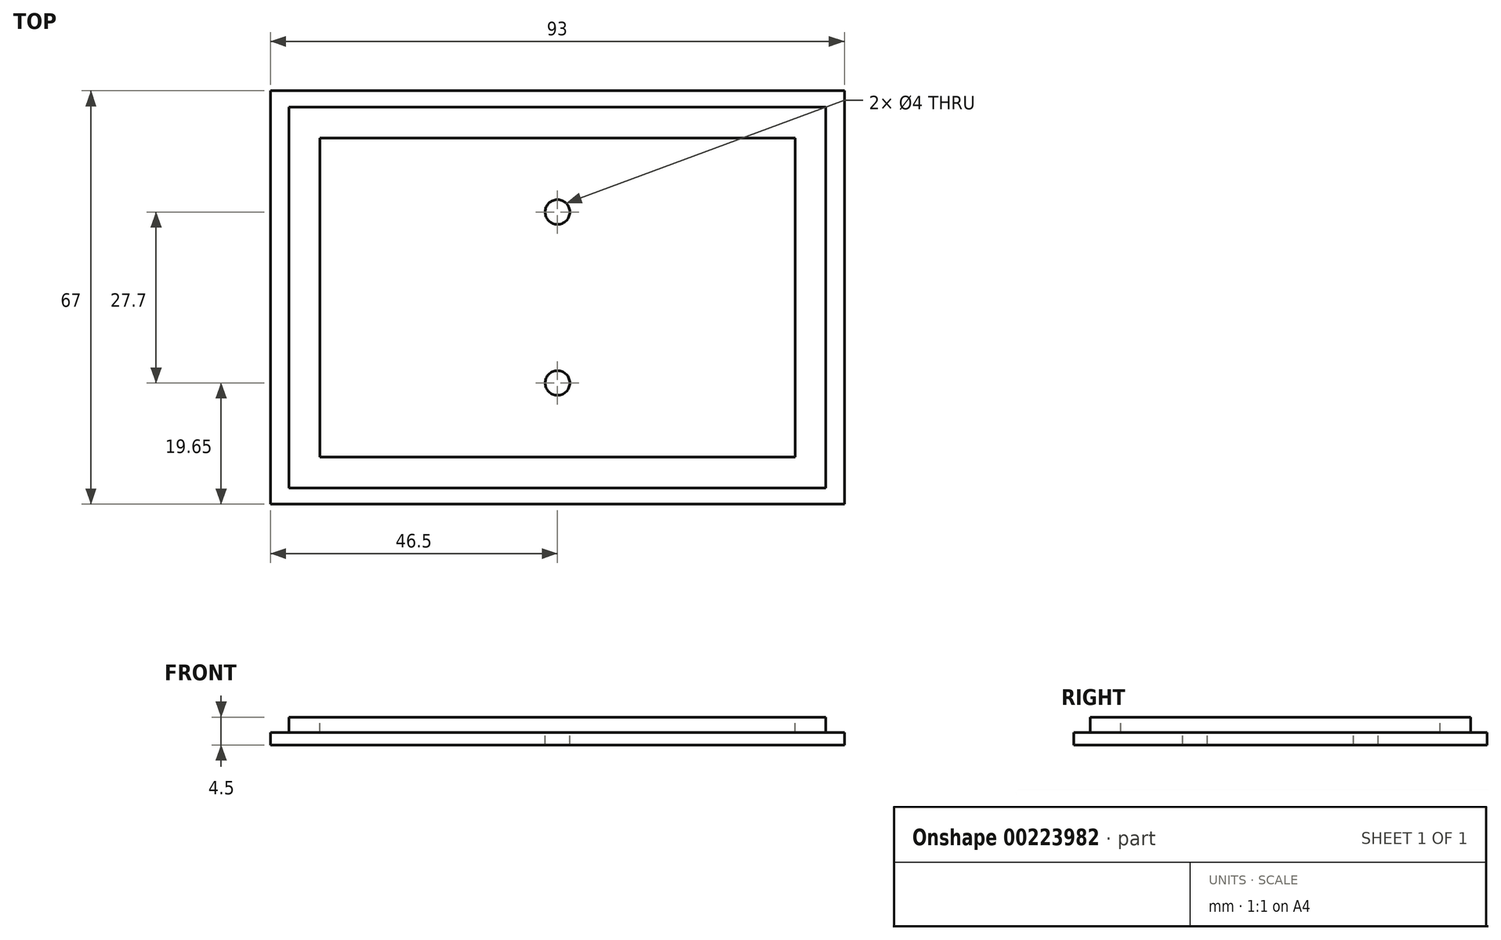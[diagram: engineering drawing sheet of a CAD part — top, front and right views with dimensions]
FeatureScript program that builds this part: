
annotation { "Feature Type Name" : "Feature", "Feature Type Description" : "" }
export const myFeature = defineFeature(function(context is Context, id is Id, definition is map)
    precondition{}
    {
        {
            var Q0;
            Q0=qCreatedBy(makeId("Top.planeOp"),FACE);
            var sketch = newSketch(context, id + "F0", { "sketchPlane" : qUnion([Q0])});
            skLineSegment(sketch, "E0.bottom", {"start": v(46.5, -33.5) * mm, "end": v(-46.5, -33.5) * mm});
            skLineSegment(sketch, "E0.top", {"start": v(46.5, 33.5) * mm, "end": v(-46.5, 33.5) * mm});
            skLineSegment(sketch, "E0.left", {"start": v(46.5, -33.5) * mm, "end": v(46.5, 33.5) * mm});
            skLineSegment(sketch, "E0.right", {"start": v(-46.5, -33.5) * mm, "end": v(-46.5, 33.5) * mm});
            skPoint(sketch, "E0.middle", {"position": v(0, 0) * mm});
            skSolve(sketch);
        }
        {
            var Q0;
            Q0 = qSketchRegion(id + "F0", true);
            extrude(context, id + "F1", {"entities" : qUnion([Q0]), "depth" : 2 * mm});
        }
        {
            var Q0;
            Q0=makeQuery(id+"F1.opExtrude","CAP_FACE",FACE,{"disambiguationData":[OSD([sQuery(id+"F0.wireOp",EDGE,"E0.bottom"),sQuery(id+"F0.wireOp",EDGE,"E0.top"),sQuery(id+"F0.wireOp",EDGE,"E0.left"),sQuery(id+"F0.wireOp",EDGE,"E0.right")])],"isStart":false});
            var sketch = newSketch(context, id + "F2", { "sketchPlane" : qUnion([Q0])});
            skLineSegment(sketch, "E1.bottom", {"start": v(43.5, -30.85) * mm, "end": v(-43.5, -30.85) * mm});
            skLineSegment(sketch, "E1.top", {"start": v(43.5, 30.85) * mm, "end": v(-43.5, 30.85) * mm});
            skLineSegment(sketch, "E1.left", {"start": v(43.5, -30.85) * mm, "end": v(43.5, 30.85) * mm});
            skLineSegment(sketch, "E1.right", {"start": v(-43.5, -30.85) * mm, "end": v(-43.5, 30.85) * mm});
            skPoint(sketch, "E1.middle", {"position": v(0, 0) * mm});
            skSolve(sketch);
        }
        {
            var Q0;
            Q0 = qSketchRegion(id + "F2", true);
            extrude(context, id + "F3", {"entities" : qUnion([Q0]), "operationType" : NewBodyOperationType.ADD, "depth" : 2.5 * mm});
        }
        {
            var Q0;
            Q0=makeQuery(id+"F3.opExtrude","CAP_FACE",FACE,{"disambiguationData":[OSD([sQuery(id+"F2.wireOp",EDGE,"E1.bottom"),sQuery(id+"F2.wireOp",EDGE,"E1.top"),sQuery(id+"F2.wireOp",EDGE,"E1.left"),sQuery(id+"F2.wireOp",EDGE,"E1.right")])],"isStart":false});
            var sketch = newSketch(context, id + "F4", { "sketchPlane" : qUnion([Q0])});
            skCircle(sketch, "E2", {"center": v(0, 13.85) * mm, "radius": 2 * mm});
            skCircle(sketch, "E3", {"center": v(0, -13.85) * mm, "radius": 2 * mm});
            skLineSegment(sketch, "E4", {"start": v(0, 30.85) * mm, "end": v(0, 15.85) * mm, "construction": true});
            skLineSegment(sketch, "E5", {"start": v(0, -30.85) * mm, "end": v(0, -15.85) * mm, "construction": true});
            skSolve(sketch);
        }
        {
            var Q0;
            Q0 = qSketchRegion(id + "F4", true);
            extrude(context, id + "F5", {"entities" : qUnion([Q0]), "operationType" : NewBodyOperationType.REMOVE, "endBound" : BoundingType.THROUGH_ALL, "oppositeDirection" : true, "depth" : 25 * mm});
        }
        {
            var Q0;
            Q0=makeQuery(id+"F3.opExtrude","CAP_FACE",FACE,{"disambiguationData":[OSD([sQuery(id+"F2.wireOp",EDGE,"E1.bottom"),sQuery(id+"F2.wireOp",EDGE,"E1.top"),sQuery(id+"F2.wireOp",EDGE,"E1.left"),sQuery(id+"F2.wireOp",EDGE,"E1.right")])],"isStart":false});
            var sketch = newSketch(context, id + "F6", { "sketchPlane" : qUnion([Q0])});
            skLineSegment(sketch, "E6.0", {"start": v(38.5, -25.85) * mm, "end": v(38.5, 25.85) * mm});
            skLineSegment(sketch, "E6.1", {"start": v(-38.5, -25.85) * mm, "end": v(38.5, -25.85) * mm});
            skLineSegment(sketch, "E6.2", {"start": v(-38.5, 25.85) * mm, "end": v(-38.5, -25.85) * mm});
            skLineSegment(sketch, "E6.3", {"start": v(38.5, 25.85) * mm, "end": v(-38.5, 25.85) * mm});
            skSolve(sketch);
        }
        {
            var Q0;
            Q0 = qSketchRegion(id + "F6", true);
            extrude(context, id + "F7", {"entities" : qUnion([Q0]), "operationType" : NewBodyOperationType.REMOVE, "oppositeDirection" : true, "depth" : 2.5 * mm});
        }
    });
